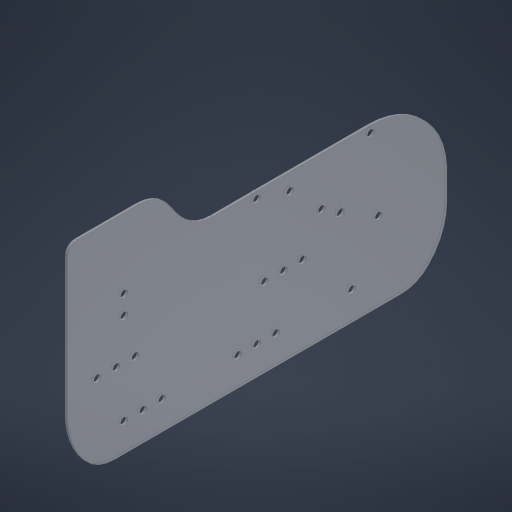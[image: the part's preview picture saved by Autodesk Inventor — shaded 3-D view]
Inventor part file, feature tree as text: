
AUTODESK INVENTOR PART (.ipt)
format: ipt  version: 2024 (Build 280153000, 153)  size: 344,576 bytes
history: native  units: in
note: dims shown in document units (in); Inventor stores cm internally (conversion verified against a paired STEP export)
features: sketch x1, extrude x1, hole x1
ambient origin geometry x8: Origin, YZ Plane, XZ Plane, XY Plane, X Axis, Y Axis, Z Axis, Center Point
bodies: Solid1 (feature_tree)
feature tree (3):
  sketch  "Sketch1"  dims[d4=0.0625in d5=0.0in d81=1.325in d82=1.5in d86=0.5in d93=1.0in d94=1.5in d95=1.5in d98=1.325in d102=0.1875in d103=0.75in d104=0.375in d105=0.25in d106=0.5635in d107=1.0in d108=0.8108in d109=1.5in d110=0.5in d111=0.5in d112=1.5in d113=1.75in d114=0.5in d115=0.5in d116=1.325in d117=1.0in d118=0.0in d119=0.25in d120=0.25in d122=0.75in d126=5.0in d127=2.5in d129=1.5in d130=0.875in d131=0.875in d132=1.5in d133=1.972in d134=1.0in d135=1.0in d137=1.25in d138=2.875in d139=1.0in d140=4.0in d141=1.5in d142=1.0in d143=0.25in d144=2.4602in d145=5.0in d153=0.25in d154=0.5in d155=0.5in d157=0.5in d158=0.25in d159=0.0625in d160=3.0in d161=0.2in d162=0.875in d163=1.5in d164=1.0in d166=1.0in]
  extrude  "Extrusion1"  Depth=1.0in
  hole  "Hole4"  [1 undecoded]
note: 1 required parameter value undecoded (feature->parameter linkage not recoverable at this tier; creation-order binding heuristic only, values carry confidence <= 0.55)
